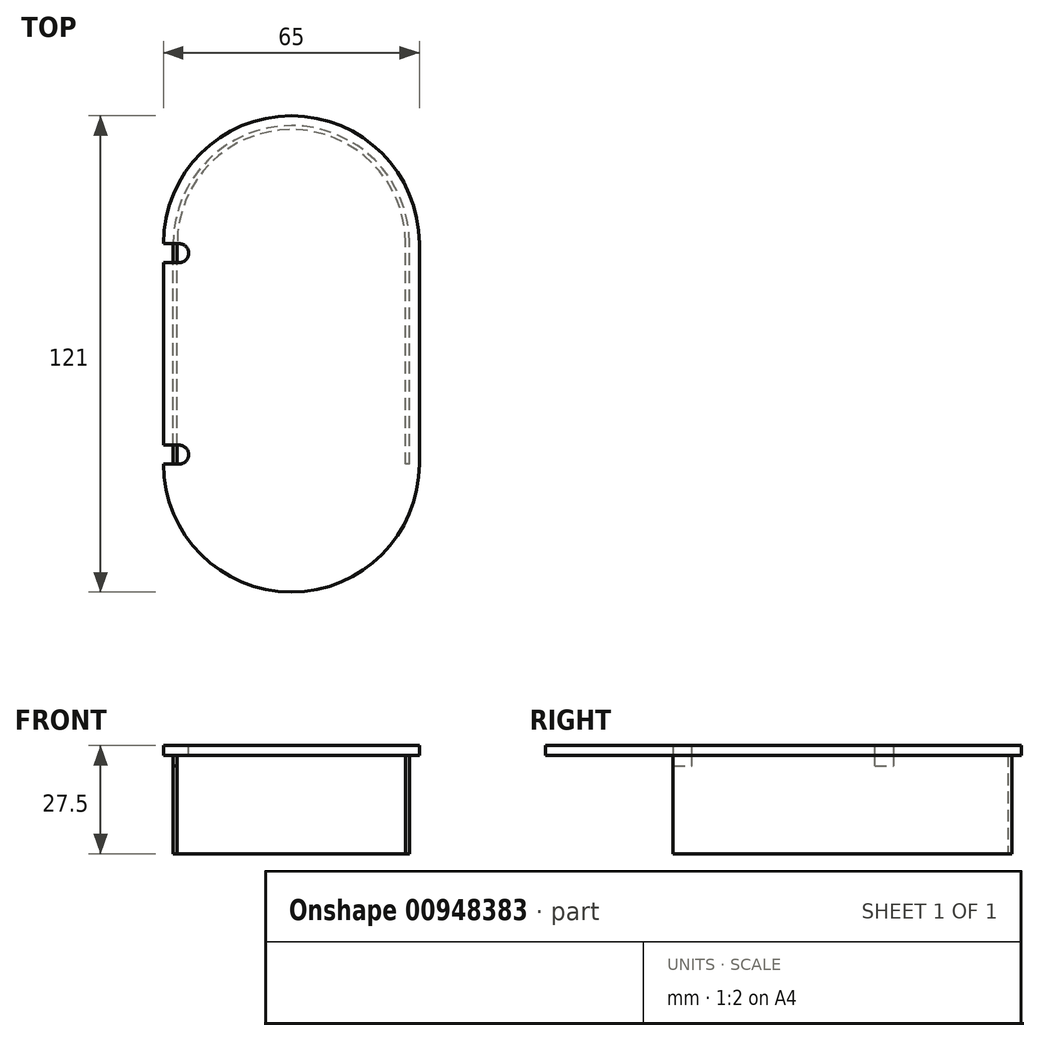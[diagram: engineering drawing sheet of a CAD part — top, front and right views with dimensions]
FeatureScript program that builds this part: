
annotation { "Feature Type Name" : "Feature", "Feature Type Description" : "" }
export const myFeature = defineFeature(function(context is Context, id is Id, definition is map)
    precondition{}
    {
        {
            var Q0;
            Q0=qCreatedBy(makeId("Top.planeOp"),FACE);
            var sketch = newSketch(context, id + "F0", { "sketchPlane" : qUnion([Q0])});
            skLineSegment(sketch, "E0", {"start": v(0, 0) * mm, "end": v(0, 56) * mm});
            skLineSegment(sketch, "E1", {"start": v(0, 0) * mm, "end": v(-60, 0) * mm});
            skLineSegment(sketch, "E2", {"start": v(-60, 0) * mm, "end": v(-60, 56) * mm});
            skArc(sketch, "E3", {"start": v(0, 0) * mm, "mid": v(-30, -30) * mm, "end": v(-60, 0) * mm});
            skArc(sketch, "E4", {"start": v(-60, 56) * mm, "mid": v(-30, 86) * mm, "end": v(0, 56) * mm});
            skLineSegment(sketch, "E5.0", {"start": v(-1, 0) * mm, "end": v(-1, 56) * mm});
            skArc(sketch, "E5.1", {"start": v(-1, 0) * mm, "mid": v(-30, -29) * mm, "end": v(-59, 0) * mm});
            skLineSegment(sketch, "E5.2", {"start": v(-59, 0) * mm, "end": v(-59, 56) * mm});
            skArc(sketch, "E5.3", {"start": v(-59, 56) * mm, "mid": v(-30, 85) * mm, "end": v(-1, 56) * mm});
            skSolve(sketch);
        }
        {
            var Q0;
            {var subQ5=sQuery(id+"F0.wireOp",EDGE,"E0");Q0=makeQuery(id+"F0.imprint","IMPRINT",FACE,{"disambiguationData":[TD([[makeQuery(id+"F0.imprint","IMPRINT",EDGE,{"derivedFrom":subQ5}),1.0]])]});}
            var Q1;
            {var subQ0=sQuery(id+"F0.wireOp",EDGE,"E3");Q1=makeQuery(id+"F0.imprint","IMPRINT",FACE,{"disambiguationData":[TD([[makeQuery(id+"F0.imprint","IMPRINT",EDGE,{"derivedFrom":subQ0}),-1.0]])]});}
            extrude(context, id + "F1", {"entities" : qUnion([Q0, Q1]), "depth" : 25 * mm, "offsetDistance" : 25 * mm});
        }
        {
            var Q0;
            Q0=makeQuery(id+"F1.opExtrude","CAP_FACE",FACE,{"disambiguationData":[OSD([sQuery(id+"F0.wireOp",EDGE,"E0"),sQuery(id+"F0.wireOp",EDGE,"E2"),sQuery(id+"F0.wireOp",EDGE,"E3"),sQuery(id+"F0.wireOp",EDGE,"E4"),sQuery(id+"F0.wireOp",EDGE,"E5.0"),sQuery(id+"F0.wireOp",EDGE,"E5.1"),sQuery(id+"F0.wireOp",EDGE,"E5.2"),sQuery(id+"F0.wireOp",EDGE,"E5.3")])],"isStart":false});
            var sketch = newSketch(context, id + "F2", { "sketchPlane" : qUnion([Q0])});
            skArc(sketch, "E6.0", {"start": v(-62.5, 56) * mm, "mid": v(-30, 88.5) * mm, "end": v(2.5, 56) * mm});
            skLineSegment(sketch, "E6.1", {"start": v(-62.5, 0) * mm, "end": v(-62.5, 56) * mm});
            skArc(sketch, "E6.2", {"start": v(2.5, 0) * mm, "mid": v(-30, -32.5) * mm, "end": v(-62.5, 0) * mm});
            skLineSegment(sketch, "E6.3", {"start": v(2.5, 0) * mm, "end": v(2.5, 56) * mm});
            skSolve(sketch);
        }
        {
            var Q0;
            Q0=makeQuery(id+"F2.imprint","IMPRINT",FACE,{"disambiguationData":[TD([[makeQuery(id+"F2.imprint","IMPRINT",EDGE,{"derivedFrom":sQuery(id+"F2.wireOp",EDGE,"E6.0")}),-1.0]])]});
            var Q1;
            Q1=makeQuery(id+"F2.imprint","IMPRINT",FACE,{"disambiguationData":[TD([[makeQuery(id+"F2.imprint","IMPRINT",EDGE,{"derivedFrom":makeQuery(id+"F1.opExtrude","CAP_EDGE",EDGE,{"disambiguationData":[OSD([sQuery(id+"F0.wireOp",EDGE,"E5.0")])],"isStart":false})}),1.0]])]});
            var Q2;
            Q2=makeQuery(id+"F2.imprint","IMPRINT",FACE,{"disambiguationData":[TD([[makeQuery(id+"F2.imprint","IMPRINT",EDGE,{"derivedFrom":makeQuery(id+"F1.opExtrude","CAP_EDGE",EDGE,{"disambiguationData":[OSD([sQuery(id+"F0.wireOp",EDGE,"E0")])],"isStart":false})}),1.0]])]});
            extrude(context, id + "F3", {"entities" : qUnion([Q0, Q1, Q2]), "operationType" : NewBodyOperationType.ADD, "depth" : 2.5 * mm, "offsetDistance" : 25 * mm});
        }
        {
            var Q0;
            Q0=makeQuery(id+"F3.opExtrude","CAP_FACE",FACE,{"disambiguationData":[OSD([sQuery(id+"F2.wireOp",EDGE,"E6.0"),sQuery(id+"F2.wireOp",EDGE,"E6.1"),sQuery(id+"F2.wireOp",EDGE,"E6.2"),sQuery(id+"F2.wireOp",EDGE,"E6.3")])],"isStart":false});
            var sketch = newSketch(context, id + "F4", { "sketchPlane" : qUnion([Q0])});
            skLineSegment(sketch, "E7", {"start": v(-62.5, 56) * mm, "end": v(-58.5, 56) * mm});
            skLineSegment(sketch, "E8", {"start": v(-62.5, 51.2) * mm, "end": v(-58.5, 51.2) * mm});
            skArc(sketch, "E9", {"start": v(-58.5, 56) * mm, "mid": v(-56.1, 53.6) * mm, "end": v(-58.5, 51.2) * mm});
            skLineSegment(sketch, "E10", {"start": v(2.5, 28) * mm, "end": v(-62.5, 28) * mm, "construction": true});
            skLineSegment(sketch, "E11.MirrorCS", {"start": v(-62.5, 0) * mm, "end": v(-58.5, 0) * mm});
            skLineSegment(sketch, "E12.MirrorCS", {"start": v(-62.5, 4.8) * mm, "end": v(-58.5, 4.8) * mm});
            skArc(sketch, "E13.MirrorCS", {"start": v(-58.5, 0) * mm, "mid": v(-56.1, 2.4) * mm, "end": v(-58.5, 4.8) * mm});
            skLineSegment(sketch, "E14", {"start": v(-62.5, 51.2) * mm, "end": v(-62.5, 4.8) * mm, "construction": true});
            skLineSegment(sketch, "E15", {"start": v(-62.5, 51.2) * mm, "end": v(-62.5, 56) * mm, "construction": true});
            skLineSegment(sketch, "E16", {"start": v(-62.5, 0) * mm, "end": v(-62.5, 4.8) * mm, "construction": true});
            skSolve(sketch);
        }
        {
            var Q0;
            {var subQ0=sQuery(id+"F4.wireOp",EDGE,"E7");Q0=makeQuery(id+"F4.imprint","IMPRINT",FACE,{"disambiguationData":[TD([[makeQuery(id+"F4.imprint","IMPRINT",EDGE,{"derivedFrom":subQ0}),-1.0]])]});}
            var Q1;
            {var subQ0=sQuery(id+"F4.wireOp",EDGE,"E11.MirrorCS");Q1=makeQuery(id+"F4.imprint","IMPRINT",FACE,{"disambiguationData":[TD([[makeQuery(id+"F4.imprint","IMPRINT",EDGE,{"derivedFrom":subQ0}),1.0]])]});}
            extrude(context, id + "F5", {"entities" : qUnion([Q0, Q1]), "operationType" : NewBodyOperationType.REMOVE, "oppositeDirection" : true, "depth" : 5.2 * mm, "offsetDistance" : 25 * mm});
        }
    });
